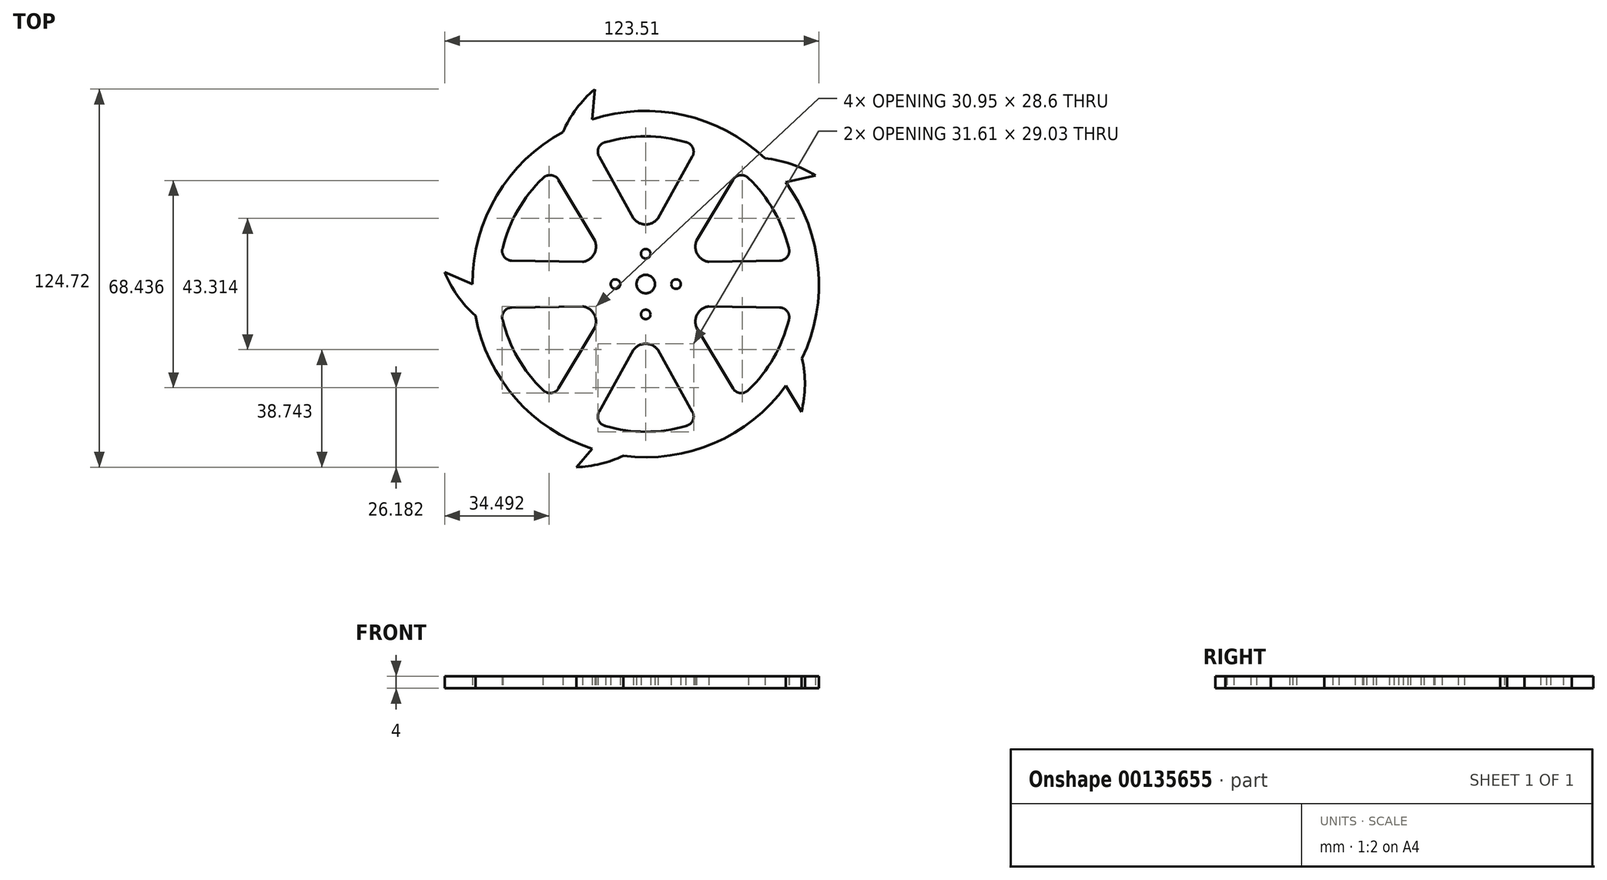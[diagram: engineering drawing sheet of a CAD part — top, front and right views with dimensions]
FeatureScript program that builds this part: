
annotation { "Feature Type Name" : "Feature", "Feature Type Description" : "" }
export const myFeature = defineFeature(function(context is Context, id is Id, definition is map)
    precondition{}
    {
        {
            var Q0;
            Q0=qCreatedBy(makeId("Top.planeOp"),FACE);
            var sketch = newSketch(context, id + "F0", { "sketchPlane" : qUnion([Q0])});
            skArc(sketch, "E0", {"start": v(-56.18, -10.47) * mm, "mid": v(-42.95, -37.7) * mm, "end": v(-17.66, -54.35) * mm});
            skLineSegment(sketch, "E1", {"start": v(-57.15, 0) * mm, "end": v(-66.36, 3.89) * mm});
            skArc(sketch, "E2", {"start": v(-66.36, 3.89) * mm, "mid": v(-62.1, -3.87) * mm, "end": v(-56.18, -10.47) * mm});
            skLineSegment(sketch, "E3.1.0", {"start": v(-17.66, -54.35) * mm, "end": v(-22.9, -60.4) * mm});
            skArc(sketch, "E3.1.1", {"start": v(-22.9, -60.4) * mm, "mid": v(-14.96, -59.33) * mm, "end": v(-7.4, -56.67) * mm});
            skLineSegment(sketch, "E3.2.0", {"start": v(46.24, -33.6) * mm, "end": v(51.4, -42.15) * mm});
            skArc(sketch, "E3.2.1", {"start": v(51.4, -42.15) * mm, "mid": v(52.5, -33.37) * mm, "end": v(51.6, -24.56) * mm});
            skLineSegment(sketch, "E3.3.0", {"start": v(46.24, 33.6) * mm, "end": v(55.97, 35.86) * mm});
            skArc(sketch, "E3.3.1", {"start": v(55.97, 35.86) * mm, "mid": v(47.96, 39.63) * mm, "end": v(39.3, 41.5) * mm});
            skLineSegment(sketch, "E3.4.0", {"start": v(-17.66, 54.35) * mm, "end": v(-16.8, 64.32) * mm});
            skArc(sketch, "E3.4.1", {"start": v(-16.8, 64.32) * mm, "mid": v(-22.87, 57.86) * mm, "end": v(-27.32, 50.2) * mm});
            skArc(sketch, "E4.trimOffspring", {"start": v(-27.32, 50.2) * mm, "mid": v(-49.13, 29.2) * mm, "end": v(-57.15, 0) * mm});
            skArc(sketch, "E5.trimOffspring", {"start": v(39.3, 41.5) * mm, "mid": v(12.59, 55.75) * mm, "end": v(-17.66, 54.35) * mm});
            skArc(sketch, "E6.trimOffspring", {"start": v(51.6, -24.56) * mm, "mid": v(56.9, 5.26) * mm, "end": v(46.24, 33.6) * mm});
            skArc(sketch, "E7.trimOffspring", {"start": v(-7.4, -56.67) * mm, "mid": v(22.58, -52.5) * mm, "end": v(46.24, -33.6) * mm});
            skCircle(sketch, "E8", {"center": v(0, 0) * mm, "radius": 3.05 * mm});
            skCircle(sketch, "E9", {"center": v(0, 10) * mm, "radius": 1.57 * mm});
            skCircle(sketch, "E10.1.0", {"center": v(-10, 0) * mm, "radius": 1.57 * mm});
            skCircle(sketch, "E10.2.0", {"center": v(0, -10) * mm, "radius": 1.57 * mm});
            skCircle(sketch, "E10.3.0", {"center": v(10, 0) * mm, "radius": 1.57 * mm});
            skLineSegment(sketch, "E11", {"start": v(4.05, 21.74) * mm, "end": v(15.4, 42.14) * mm});
            skLineSegment(sketch, "E12.MirrorCS", {"start": v(-4.05, 21.74) * mm, "end": v(-15.4, 42.14) * mm});
            skArc(sketch, "E13", {"start": v(-4.05, 21.74) * mm, "mid": v(0, 19.7) * mm, "end": v(4.05, 21.74) * mm});
            skArc(sketch, "E14", {"start": v(-13.25, 46.84) * mm, "mid": v(-15.52, 45.04) * mm, "end": v(-15.4, 42.14) * mm});
            skArc(sketch, "E15.MirrorCS", {"start": v(13.25, 46.84) * mm, "mid": v(15.52, 45.04) * mm, "end": v(15.4, 42.14) * mm});
            skArc(sketch, "E16", {"start": v(13.25, 46.84) * mm, "mid": v(0, 48.73) * mm, "end": v(-13.25, 46.84) * mm});
            skArc(sketch, "E17.1.0", {"start": v(-33.94, 34.9) * mm, "mid": v(-31.24, 35.96) * mm, "end": v(-28.8, 34.41) * mm});
            skLineSegment(sketch, "E17.1.1", {"start": v(-20.85, 7.36) * mm, "end": v(-44.2, 7.73) * mm});
            skArc(sketch, "E17.1.2", {"start": v(-33.94, 34.9) * mm, "mid": v(-42.2, 24.37) * mm, "end": v(-47.2, 11.94) * mm});
            skArc(sketch, "E17.1.3", {"start": v(-20.85, 7.36) * mm, "mid": v(-17.06, 9.85) * mm, "end": v(-16.8, 14.38) * mm});
            skArc(sketch, "E17.1.4", {"start": v(-47.2, 11.94) * mm, "mid": v(-46.76, 9.08) * mm, "end": v(-44.2, 7.73) * mm});
            skLineSegment(sketch, "E17.1.5", {"start": v(-16.8, 14.38) * mm, "end": v(-28.8, 34.41) * mm});
            skArc(sketch, "E17.2.0", {"start": v(-47.2, -11.94) * mm, "mid": v(-46.76, -9.08) * mm, "end": v(-44.2, -7.73) * mm});
            skLineSegment(sketch, "E17.2.1", {"start": v(-16.8, -14.38) * mm, "end": v(-28.8, -34.41) * mm});
            skArc(sketch, "E17.2.2", {"start": v(-47.2, -11.94) * mm, "mid": v(-42.2, -24.37) * mm, "end": v(-33.94, -34.9) * mm});
            skArc(sketch, "E17.2.3", {"start": v(-16.8, -14.38) * mm, "mid": v(-17.06, -9.85) * mm, "end": v(-20.85, -7.36) * mm});
            skArc(sketch, "E17.2.4", {"start": v(-33.94, -34.9) * mm, "mid": v(-31.24, -35.96) * mm, "end": v(-28.8, -34.41) * mm});
            skLineSegment(sketch, "E17.2.5", {"start": v(-20.85, -7.36) * mm, "end": v(-44.2, -7.73) * mm});
            skArc(sketch, "E17.3.0", {"start": v(-13.25, -46.84) * mm, "mid": v(-15.52, -45.04) * mm, "end": v(-15.4, -42.14) * mm});
            skLineSegment(sketch, "E17.3.1", {"start": v(4.05, -21.74) * mm, "end": v(15.4, -42.14) * mm});
            skArc(sketch, "E17.3.2", {"start": v(-13.25, -46.84) * mm, "mid": v(0, -48.73) * mm, "end": v(13.25, -46.84) * mm});
            skArc(sketch, "E17.3.3", {"start": v(4.05, -21.74) * mm, "mid": v(0, -19.7) * mm, "end": v(-4.05, -21.74) * mm});
            skArc(sketch, "E17.3.4", {"start": v(13.25, -46.84) * mm, "mid": v(15.52, -45.04) * mm, "end": v(15.4, -42.14) * mm});
            skLineSegment(sketch, "E17.3.5", {"start": v(-4.05, -21.74) * mm, "end": v(-15.4, -42.14) * mm});
            skArc(sketch, "E17.4.0", {"start": v(33.94, -34.9) * mm, "mid": v(31.24, -35.96) * mm, "end": v(28.8, -34.41) * mm});
            skLineSegment(sketch, "E17.4.1", {"start": v(20.85, -7.36) * mm, "end": v(44.2, -7.73) * mm});
            skArc(sketch, "E17.4.2", {"start": v(33.94, -34.9) * mm, "mid": v(42.2, -24.37) * mm, "end": v(47.2, -11.94) * mm});
            skArc(sketch, "E17.4.3", {"start": v(20.85, -7.36) * mm, "mid": v(17.06, -9.85) * mm, "end": v(16.8, -14.38) * mm});
            skArc(sketch, "E17.4.4", {"start": v(47.2, -11.94) * mm, "mid": v(46.76, -9.08) * mm, "end": v(44.2, -7.73) * mm});
            skLineSegment(sketch, "E17.4.5", {"start": v(16.8, -14.38) * mm, "end": v(28.8, -34.41) * mm});
            skLineSegment(sketch, "E18.4.5.0", {"start": v(16.8, 14.38) * mm, "end": v(28.8, 34.41) * mm});
            skArc(sketch, "E18.7.5.0", {"start": v(47.2, 11.94) * mm, "mid": v(42.2, 24.37) * mm, "end": v(33.94, 34.9) * mm});
            skArc(sketch, "E18.8.5.0", {"start": v(47.2, 11.94) * mm, "mid": v(46.76, 9.08) * mm, "end": v(44.2, 7.73) * mm});
            skArc(sketch, "E18.11.5.0", {"start": v(16.8, 14.38) * mm, "mid": v(17.06, 9.85) * mm, "end": v(20.85, 7.36) * mm});
            skArc(sketch, "E18.15.5.0", {"start": v(33.94, 34.9) * mm, "mid": v(31.24, 35.96) * mm, "end": v(28.8, 34.41) * mm});
            skLineSegment(sketch, "E18.19.5.0", {"start": v(20.85, 7.36) * mm, "end": v(44.2, 7.73) * mm});
            skSolve(sketch);
        }
        {
            var Q0;
            Q0=makeQuery(id+"F0.imprint","IMPRINT",FACE,{"disambiguationData":[TD([[makeQuery(id+"F0.imprint","IMPRINT",EDGE,{"derivedFrom":sQuery(id+"F0.wireOp",EDGE,"E0")}),1.0]])]});
            extrude(context, id + "F1", {"entities" : qUnion([Q0]), "depth" : 4 * mm});
        }
    });
